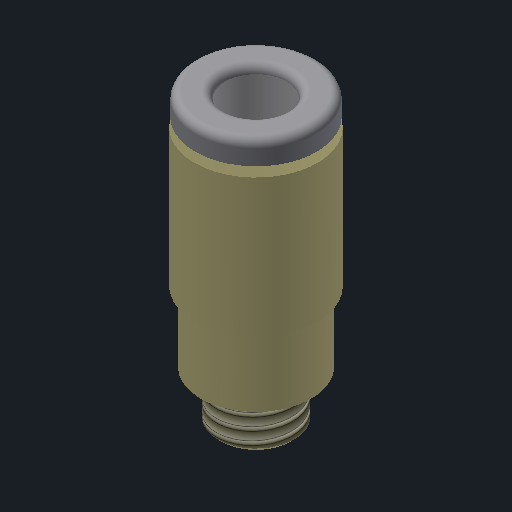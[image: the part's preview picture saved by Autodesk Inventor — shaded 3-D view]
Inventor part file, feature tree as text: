
AUTODESK INVENTOR PART (.ipt)
format: ipt  version: 2024 (Build 280153000, 153)  size: 191,488 bytes
history: native  units: in
note: dims shown in document units (in); Inventor stores cm internally (conversion verified against a paired STEP export)
features: other x1, imported_body x1, thread x1
ambient origin geometry x8: Origin, YZ Plane, XZ Plane, XY Plane, X Axis, Y Axis, Z Axis, Center Point
bodies: Body1 (feature_tree)
feature tree (3):
  other  "Port"
  imported_body  "Base1"
  thread  "Thread1"  [1 undecoded]
note: 1 required parameter value undecoded (feature->parameter linkage not recoverable at this tier; creation-order binding heuristic only, values carry confidence <= 0.55)
